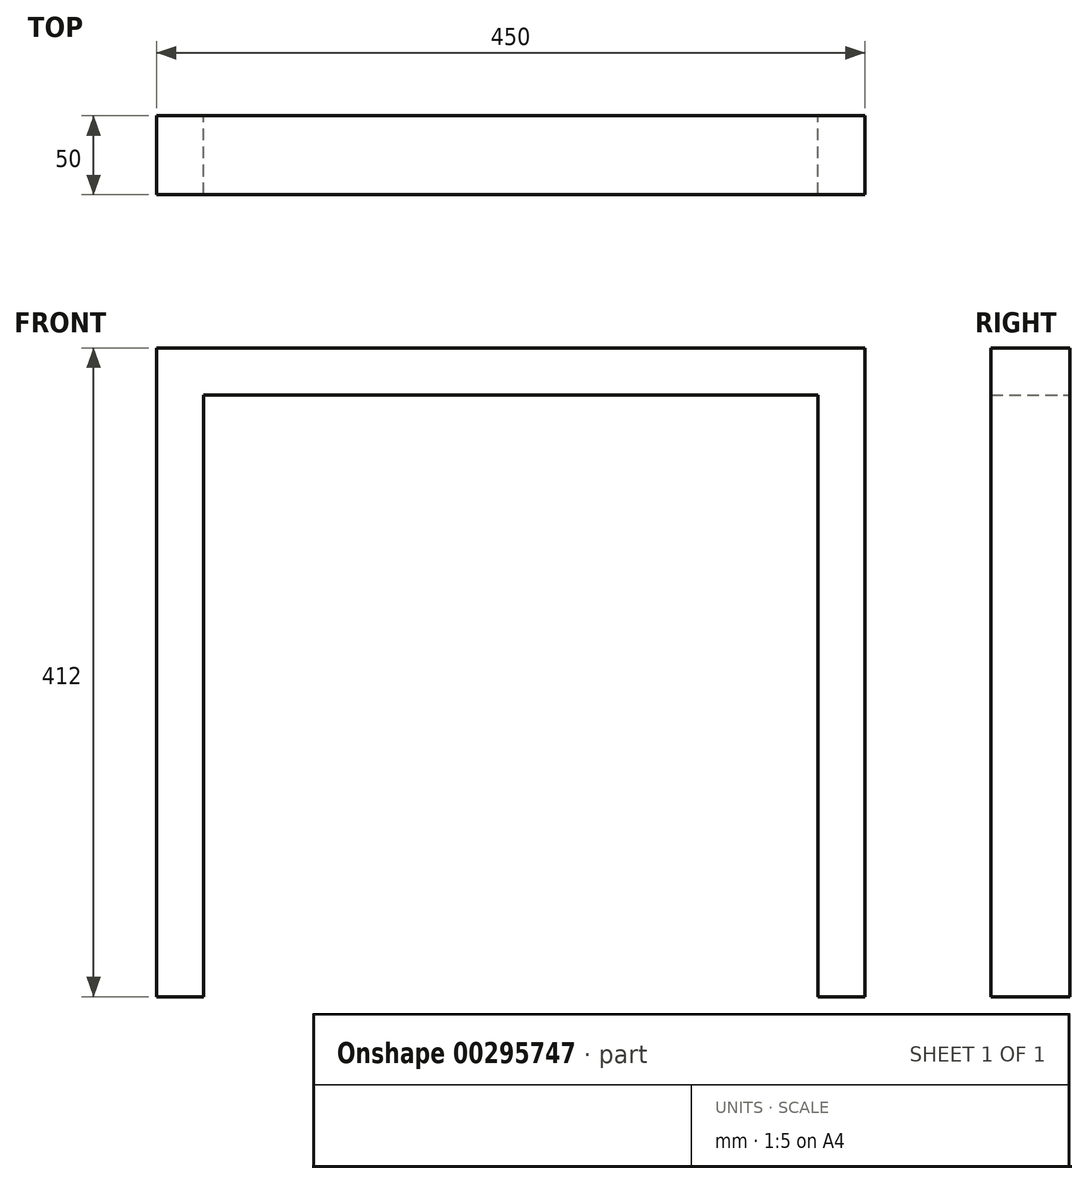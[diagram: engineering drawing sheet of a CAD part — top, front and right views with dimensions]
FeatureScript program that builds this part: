
annotation { "Feature Type Name" : "Feature", "Feature Type Description" : "" }
export const myFeature = defineFeature(function(context is Context, id is Id, definition is map)
    precondition{}
    {
        {
            var Q0;
            Q0=qCreatedBy(makeId("Front.planeOp"),FACE);
            var sketch = newSketch(context, id + "F0", { "sketchPlane" : qUnion([Q0])});
            skLineSegment(sketch, "E0.bottom", {"start": v(-251.9, 249.92) * mm, "end": v(198.1, 249.92) * mm});
            skLineSegment(sketch, "E0.left", {"start": v(-251.9, 249.92) * mm, "end": v(-251.9, -162.08) * mm});
            skLineSegment(sketch, "E0.right", {"start": v(198.1, 249.92) * mm, "end": v(198.1, -162.08) * mm});
            skLineSegment(sketch, "E1.bottom", {"start": v(-221.9, 219.92) * mm, "end": v(168.1, 219.92) * mm});
            skLineSegment(sketch, "E1.left", {"start": v(-221.9, 219.92) * mm, "end": v(-221.9, -162.08) * mm});
            skLineSegment(sketch, "E1.right", {"start": v(168.1, 219.92) * mm, "end": v(168.1, -162.08) * mm});
            skLineSegment(sketch, "E2", {"start": v(-221.9, -162.08) * mm, "end": v(-251.9, -162.08) * mm});
            skLineSegment(sketch, "E3", {"start": v(168.1, -162.08) * mm, "end": v(198.1, -162.08) * mm});
            skSolve(sketch);
        }
        {
            var Q0;
            Q0=qSketchRegion(id+"F0",true);
            extrude(context, id + "F1", {"entities" : qUnion([Q0]), "depth" : 50 * mm});
        }
    });
